# Revit family: РИДАН_Термостатические элементы серии TR 8000
name_source: partatom
category: Арматура трубопроводов
units: mm (PartAtom-declared; Revit-internal decimal feet)

## family parameters
Всегда вертикально = Да
На основе рабочей плоскости = Нет
Общий = Да
При загрузке вырезать с полостями = Нет
Размер круглого соединителя = Использовать диаметр
Тип детали = Нормальный

## types (2) — shared parameters
ADSK_Версия Revit = 2019
ADSK_Версия семейства = 1.0
ADSK_Единица измерения = шт.
ADSK_Завод-изготовитель = ООО «Ридан-Трейд»
ADSK_Количество = 1
ADSK_Материал = <По категории>
LT = TR8000
zero-valued in all types: ADSK_Масса

## per-type parameters (varying)
| type | ADSK_Код изделия | ADSK_Наименование | RA | Артикул | Гайка |
| TR 8000 | 013G8000R | Термостатический элемент со встроенным датчиком, присоединение RTR/RA | Да | 013G8000R | Нет |
| TR 8001 | 013G8001R | Термостатический элемент со встроенным датчиком, присоединение М30х1,5 | Нет | 013G8001R | Да |

note: column(s) folded — value = type name in every type: ADSK_Марка
